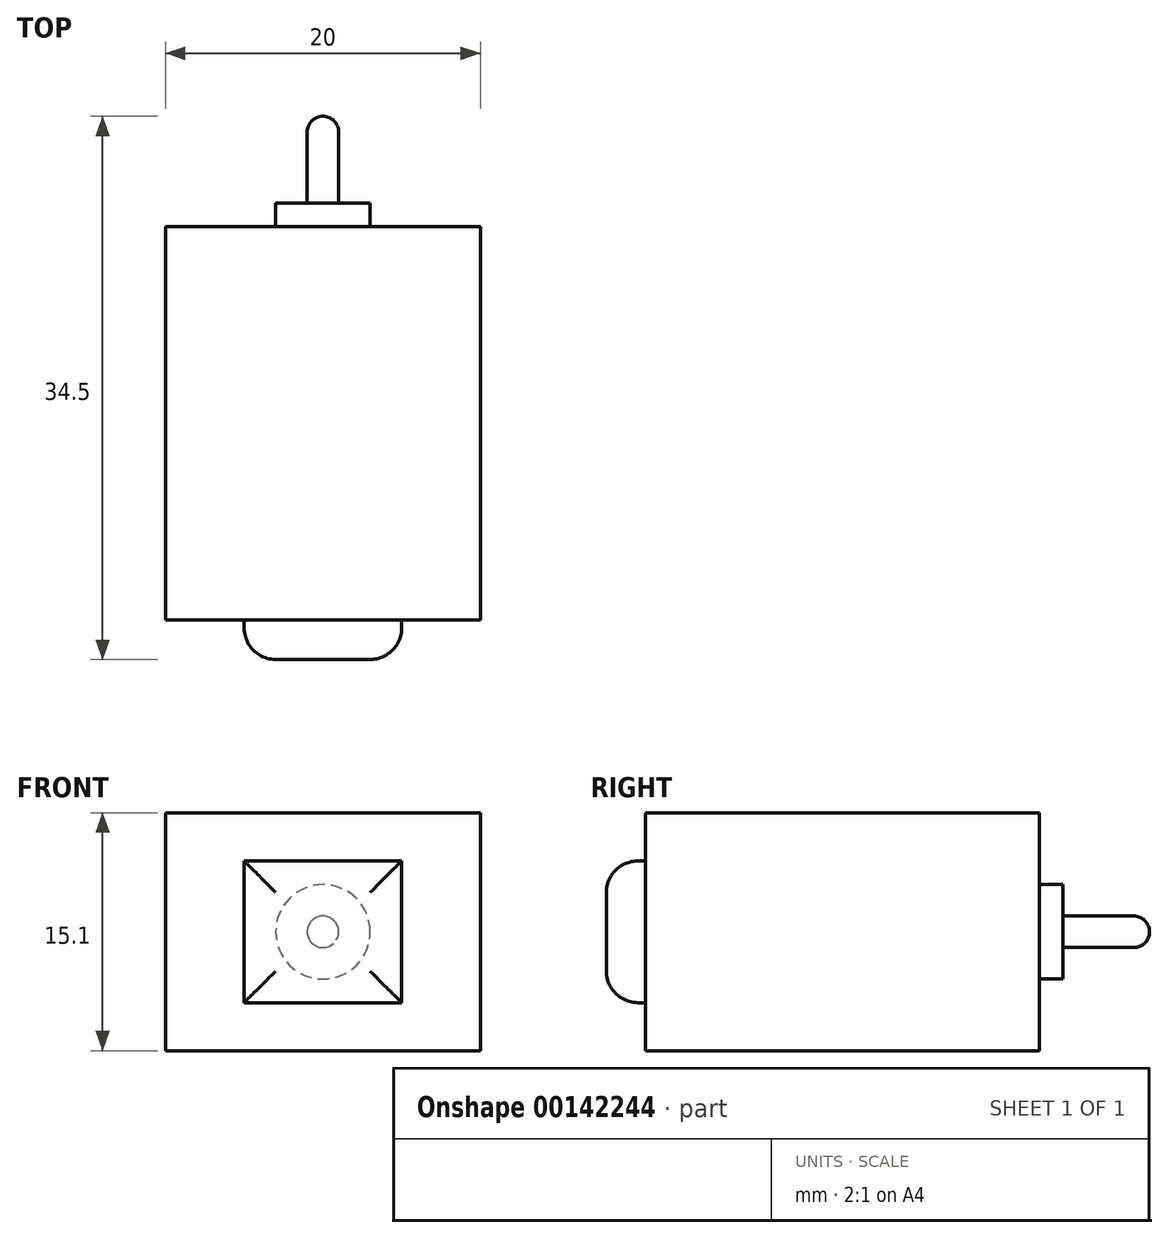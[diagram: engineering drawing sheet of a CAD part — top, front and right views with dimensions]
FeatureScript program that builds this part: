
annotation { "Feature Type Name" : "Feature", "Feature Type Description" : "" }
export const myFeature = defineFeature(function(context is Context, id is Id, definition is map)
    precondition{}
    {
        {
            var Q0;
            Q0=qCreatedBy(makeId("Front.planeOp"),FACE);
            var sketch = newSketch(context, id + "F0", { "sketchPlane" : qUnion([Q0])});
            skLineSegment(sketch, "E0.bottom", {"start": v(10, -7.55) * mm, "end": v(-10, -7.55) * mm});
            skLineSegment(sketch, "E0.top", {"start": v(10, 7.55) * mm, "end": v(-10, 7.55) * mm});
            skLineSegment(sketch, "E0.left", {"start": v(10, -7.55) * mm, "end": v(10, 7.55) * mm});
            skLineSegment(sketch, "E0.right", {"start": v(-10, -7.55) * mm, "end": v(-10, 7.55) * mm});
            skPoint(sketch, "E0.middle", {"position": v(0, 0) * mm});
            skSolve(sketch);
        }
        {
            var Q0;
            Q0=makeQuery(id+"F0.imprint","IMPRINT",FACE,{"disambiguationData":[TD([[makeQuery(id+"F0.imprint","IMPRINT",EDGE,{"derivedFrom":sQuery(id+"F0.wireOp",EDGE,"E0.bottom")}),-1.0]])]});
            extrude(context, id + "F1", {"entities" : qUnion([Q0]), "depth" : 25 * mm});
        }
        {
            var Q0;
            Q0=makeQuery(id+"F1.opExtrude","CAP_FACE",FACE,{"disambiguationData":[OSD([sQuery(id+"F0.wireOp",EDGE,"E0.bottom"),sQuery(id+"F0.wireOp",EDGE,"E0.top"),sQuery(id+"F0.wireOp",EDGE,"E0.left"),sQuery(id+"F0.wireOp",EDGE,"E0.right")])],"isStart":true});
            cPlane(context, id + "F2", {"entities" : qUnion([Q0]), "cplaneType" : CPlaneType.OFFSET, "offset" : 0 * mm, "width" : 150 * mm, "height" : 150 * mm});
        }
        {
            var Q0;
            Q0=qCreatedBy(id+"F2.planeOp",FACE);
            var sketch = newSketch(context, id + "F3", { "sketchPlane" : qUnion([Q0])});
            skCircle(sketch, "E1", {"center": v(0, 0) * mm, "radius": 3 * mm});
            skCircle(sketch, "E2", {"center": v(0, 0) * mm, "radius": 1 * mm});
            skSolve(sketch);
        }
        {
            var Q0;
            Q0=makeQuery(id+"F3.imprint","IMPRINT",FACE,{"disambiguationData":[TD([[makeQuery(id+"F3.imprint","IMPRINT",EDGE,{"derivedFrom":sQuery(id+"F3.wireOp",EDGE,"E1")}),1.0]])]});
            extrude(context, id + "F4", {"entities" : qUnion([Q0]), "operationType" : NewBodyOperationType.ADD, "depth" : 1.5 * mm});
        }
        {
            var Q0;
            Q0=makeQuery(id+"F4.boolean.opBoolean","SPLIT",FACE,{"disambiguationData":[TD([makeQuery(id+"F4.opExtrude","SWEPT_FACE",FACE,{"disambiguationData":[OSD([sQuery(id+"F3.wireOp",EDGE,"E2")])]})])],"derivedFrom":makeQuery(id+"F1.opExtrude","CAP_FACE",FACE,{"disambiguationData":[OSD([sQuery(id+"F0.wireOp",EDGE,"E0.bottom"),sQuery(id+"F0.wireOp",EDGE,"E0.top"),sQuery(id+"F0.wireOp",EDGE,"E0.left"),sQuery(id+"F0.wireOp",EDGE,"E0.right")])],"isStart":true})});
            extrude(context, id + "F5", {"entities" : qUnion([Q0]), "operationType" : NewBodyOperationType.ADD, "depth" : 7 * mm});
        }
        {
            var Q0;
            Q0=makeQuery(id+"F5.opExtrude","CAP_EDGE",EDGE,{"disambiguationData":[OSD([sQuery(id+"F3.wireOp",EDGE,"E2")])],"isStart":false});
            fillet(context, id + "F6", {"entities" : qUnion([Q0]), "radius" : 1 * mm, "tangentPropagation" : true, "allowEdgeOverflow" : false});
        }
        {
            var Q0;
            Q0=makeQuery(id+"F1.opExtrude","CAP_FACE",FACE,{"disambiguationData":[OSD([sQuery(id+"F0.wireOp",EDGE,"E0.bottom"),sQuery(id+"F0.wireOp",EDGE,"E0.top"),sQuery(id+"F0.wireOp",EDGE,"E0.left"),sQuery(id+"F0.wireOp",EDGE,"E0.right")])],"isStart":false});
            cPlane(context, id + "F7", {"entities" : qUnion([Q0]), "cplaneType" : CPlaneType.OFFSET, "offset" : 0 * mm, "width" : 150 * mm, "height" : 150 * mm});
        }
        {
            var Q0;
            Q0=qCreatedBy(id+"F7.planeOp",FACE);
            var sketch = newSketch(context, id + "F8", { "sketchPlane" : qUnion([Q0])});
            skLineSegment(sketch, "E3.bottom", {"start": v(5, -4.5) * mm, "end": v(-5, -4.5) * mm});
            skLineSegment(sketch, "E3.top", {"start": v(5, 4.5) * mm, "end": v(-5, 4.5) * mm});
            skLineSegment(sketch, "E3.left", {"start": v(5, -4.5) * mm, "end": v(5, 4.5) * mm});
            skLineSegment(sketch, "E3.right", {"start": v(-5, -4.5) * mm, "end": v(-5, 4.5) * mm});
            skPoint(sketch, "E3.middle", {"position": v(0, 0) * mm});
            skSolve(sketch);
        }
        {
            var Q0;
            Q0=makeQuery(id+"F8.imprint","IMPRINT",FACE,{"disambiguationData":[TD([[makeQuery(id+"F8.imprint","IMPRINT",EDGE,{"derivedFrom":sQuery(id+"F8.wireOp",EDGE,"E3.bottom")}),-1.0]])]});
            extrude(context, id + "F9", {"entities" : qUnion([Q0]), "operationType" : NewBodyOperationType.ADD, "depth" : 2.5 * mm});
        }
        {
            var Q0;
            Q0=makeQuery(id+"F9.opExtrude","CAP_EDGE",EDGE,{"disambiguationData":[OSD([sQuery(id+"F8.wireOp",EDGE,"E3.top")])],"isStart":false});
            var Q1;
            Q1=makeQuery(id+"F9.opExtrude","CAP_EDGE",EDGE,{"disambiguationData":[OSD([sQuery(id+"F8.wireOp",EDGE,"E3.left")])],"isStart":false});
            var Q2;
            Q2=makeQuery(id+"F9.opExtrude","CAP_EDGE",EDGE,{"disambiguationData":[OSD([sQuery(id+"F8.wireOp",EDGE,"E3.right")])],"isStart":false});
            var Q3;
            Q3=makeQuery(id+"F9.opExtrude","CAP_EDGE",EDGE,{"disambiguationData":[OSD([sQuery(id+"F8.wireOp",EDGE,"E3.bottom")])],"isStart":false});
            fillet(context, id + "F10", {"entities" : qUnion([Q0, Q1, Q2, Q3]), "radius" : 2 * mm, "tangentPropagation" : true, "allowEdgeOverflow" : false});
        }
    });
